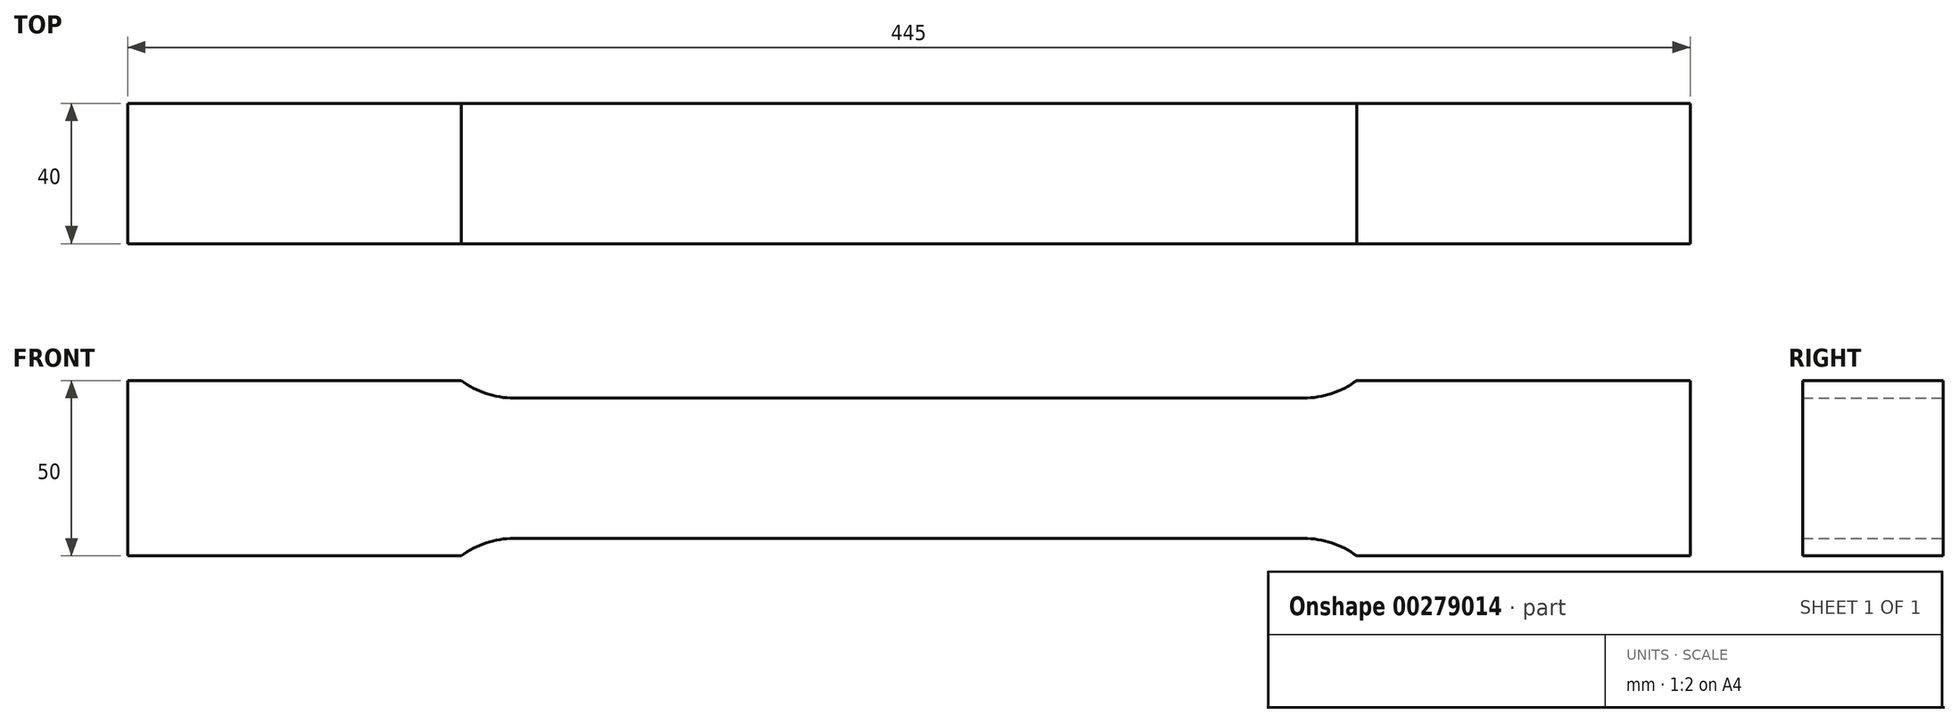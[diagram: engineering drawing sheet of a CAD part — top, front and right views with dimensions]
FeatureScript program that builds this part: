
annotation { "Feature Type Name" : "Feature", "Feature Type Description" : "" }
export const myFeature = defineFeature(function(context is Context, id is Id, definition is map)
    precondition{}
    {
        {
            var Q0;
            Q0=qCreatedBy(makeId("Front.planeOp"),FACE);
            var sketch = newSketch(context, id + "F0", { "sketchPlane" : qUnion([Q0])});
            skLineSegment(sketch, "E0", {"start": v(0, 20) * mm, "end": v(112.5, 20) * mm});
            skArc(sketch, "E1", {"start": v(112.5, 20) * mm, "mid": v(120.4, 21.28) * mm, "end": v(127.5, 25) * mm});
            skLineSegment(sketch, "E2", {"start": v(127.5, 25) * mm, "end": v(222.5, 25) * mm});
            skLineSegment(sketch, "E3", {"start": v(222.5, 25) * mm, "end": v(222.5, 0) * mm});
            skLineSegment(sketch, "E4.MirrorCS", {"start": v(0, -20) * mm, "end": v(112.5, -20) * mm});
            skLineSegment(sketch, "E5.MirrorCS", {"start": v(222.5, -25) * mm, "end": v(222.5, 0) * mm});
            skLineSegment(sketch, "E6.MirrorCS", {"start": v(127.5, -25) * mm, "end": v(222.5, -25) * mm});
            skArc(sketch, "E7.MirrorCS", {"start": v(112.5, -20) * mm, "mid": v(120.4, -21.28) * mm, "end": v(127.5, -25) * mm});
            skArc(sketch, "E8.MirrorCS", {"start": v(-112.5, -20) * mm, "mid": v(-120.4, -21.28) * mm, "end": v(-127.5, -25) * mm});
            skLineSegment(sketch, "E9.MirrorCS", {"start": v(-127.5, -25) * mm, "end": v(-222.5, -25) * mm});
            skArc(sketch, "E10.MirrorCS", {"start": v(-112.5, 20) * mm, "mid": v(-120.4, 21.28) * mm, "end": v(-127.5, 25) * mm});
            skLineSegment(sketch, "E11.MirrorCS", {"start": v(-127.5, 25) * mm, "end": v(-222.5, 25) * mm});
            skLineSegment(sketch, "E12.MirrorCS", {"start": v(-222.5, -25) * mm, "end": v(-222.5, 0) * mm});
            skLineSegment(sketch, "E13.MirrorCS", {"start": v(0, -20) * mm, "end": v(-112.5, -20) * mm});
            skLineSegment(sketch, "E14.MirrorCS", {"start": v(-222.5, 25) * mm, "end": v(-222.5, 0) * mm});
            skLineSegment(sketch, "E15.MirrorCS", {"start": v(0, 20) * mm, "end": v(-112.5, 20) * mm});
            skSolve(sketch);
        }
        {
            var Q0;
            Q0=makeQuery(id+"F0.imprint","IMPRINT",FACE,{"disambiguationData":[TD([[makeQuery(id+"F0.imprint","IMPRINT",EDGE,{"derivedFrom":sQuery(id+"F0.wireOp",EDGE,"E0")}),-1.0]])]});
            extrude(context, id + "F1", {"entities" : qUnion([Q0]), "endBound" : BoundingType.SYMMETRIC, "depth" : 40 * mm});
        }
    });
